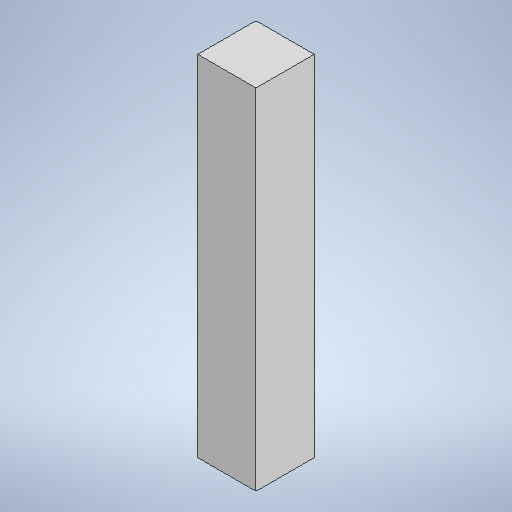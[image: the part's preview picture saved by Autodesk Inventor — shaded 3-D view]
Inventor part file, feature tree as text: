
AUTODESK INVENTOR PART (.ipt)
format: ipt  version: 2025.2 (Build 292293000, 293)  size: 227,840 bytes
history: native  units: in
note: dims shown in document units (in); Inventor stores cm internally (conversion verified against a paired STEP export)
features: extrude x1, sketch x1
ambient origin geometry x8: Origin, YZ Plane, XZ Plane, XY Plane, X Axis, Y Axis, Z Axis, Center Point
bodies: Solid1 (feature_tree)
feature tree (2):
  extrude  "Extrusion1"  Depth=0.2362in
  sketch  "Sketch1"  dims[d0=0.2362in d1=0.2362in d2=1.4173in d3=0.0in]
